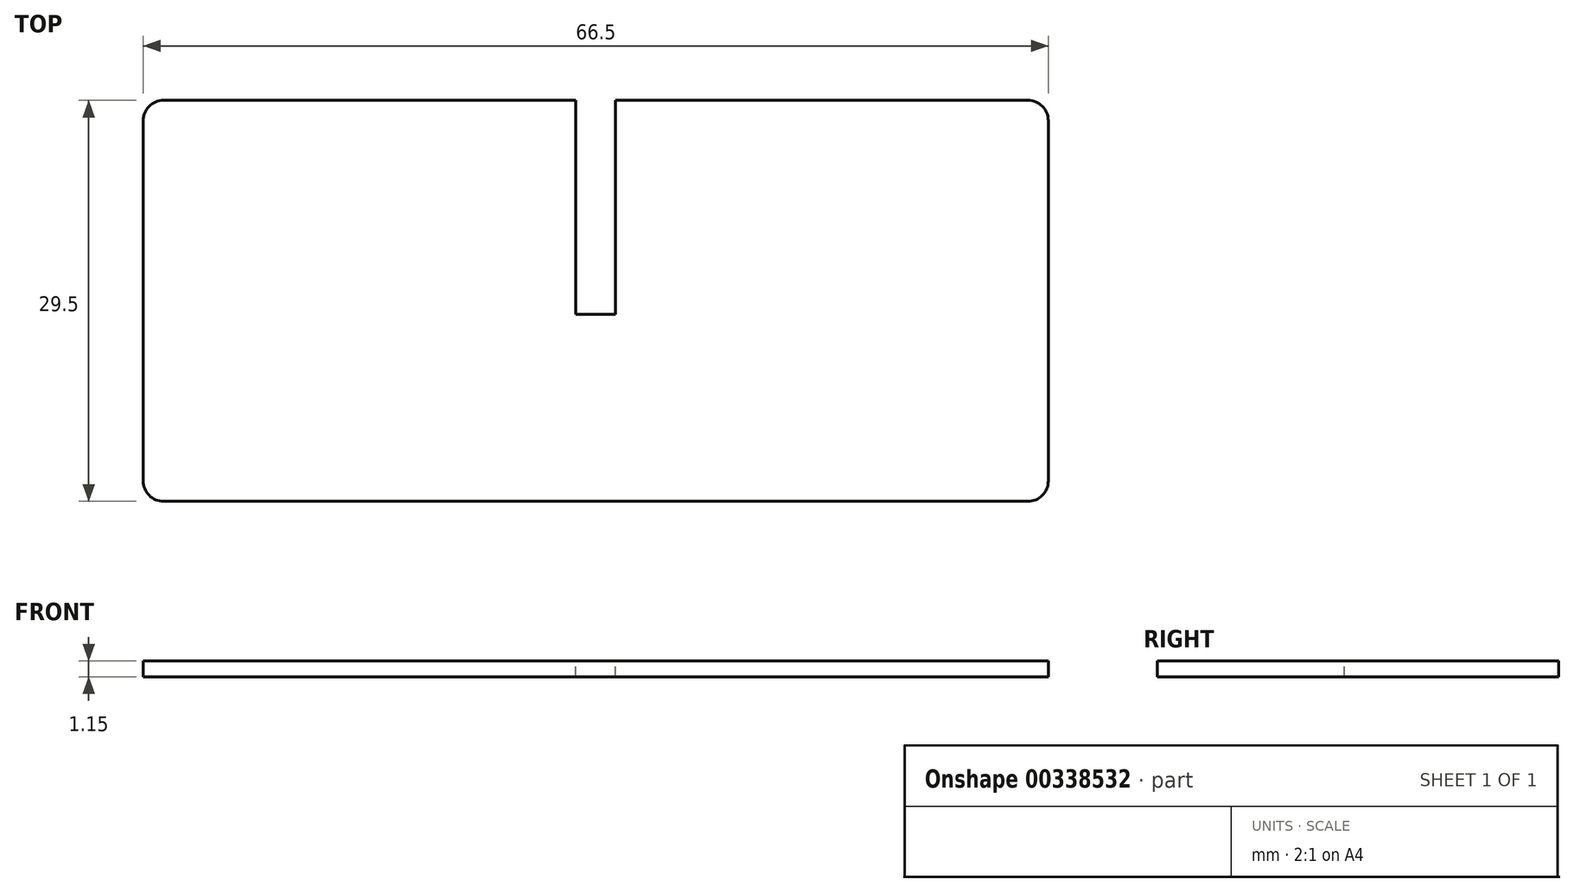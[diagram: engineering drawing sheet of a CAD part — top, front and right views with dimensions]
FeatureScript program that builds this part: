
annotation { "Feature Type Name" : "Feature", "Feature Type Description" : "" }
export const myFeature = defineFeature(function(context is Context, id is Id, definition is map)
    precondition{}
    {
        {
            var Q0;
            Q0=qCreatedBy(makeId("Top.planeOp"),FACE);
            var sketch = newSketch(context, id + "F0", { "sketchPlane" : qUnion([Q0])});
            skLineSegment(sketch, "E0.bottom", {"start": v(31.75, 14.75) * mm, "end": v(-31.75, 14.75) * mm});
            skLineSegment(sketch, "E0.top", {"start": v(31.75, -14.75) * mm, "end": v(-31.75, -14.75) * mm});
            skLineSegment(sketch, "E0.left", {"start": v(33.25, 13.25) * mm, "end": v(33.25, -13.25) * mm});
            skLineSegment(sketch, "E0.right", {"start": v(-33.25, 13.25) * mm, "end": v(-33.25, -13.25) * mm});
            skPoint(sketch, "E0.middle", {"position": v(0, 0) * mm});
            skPoint(sketch, "E1.visualSharp", {"position": v(-33.25, 14.75) * mm});
            skArc(sketch, "E1.filletArc", {"start": v(-31.75, 14.75) * mm, "mid": v(-32.81, 14.31) * mm, "end": v(-33.25, 13.25) * mm});
            skPoint(sketch, "E2.visualSharp", {"position": v(33.25, 14.75) * mm});
            skArc(sketch, "E2.filletArc", {"start": v(33.25, 13.25) * mm, "mid": v(32.81, 14.31) * mm, "end": v(31.75, 14.75) * mm});
            skPoint(sketch, "E3.visualSharp", {"position": v(33.25, -14.75) * mm});
            skArc(sketch, "E3.filletArc", {"start": v(31.75, -14.75) * mm, "mid": v(32.81, -14.31) * mm, "end": v(33.25, -13.25) * mm});
            skPoint(sketch, "E4.visualSharp", {"position": v(-33.25, -14.75) * mm});
            skArc(sketch, "E4.filletArc", {"start": v(-33.25, -13.25) * mm, "mid": v(-32.81, -14.31) * mm, "end": v(-31.75, -14.75) * mm});
            skSolve(sketch);
        }
        {
            var Q0;
            Q0=makeQuery(id+"F0.imprint","IMPRINT",FACE,{"disambiguationData":[TD([[makeQuery(id+"F0.imprint","IMPRINT",EDGE,{"derivedFrom":sQuery(id+"F0.wireOp",EDGE,"E0.bottom")}),1.0]])]});
            extrude(context, id + "F1", {"entities" : qUnion([Q0]), "depth" : 1.15 * mm});
        }
        {
            var Q0;
            Q0=makeQuery(id+"F1.opExtrude","CAP_FACE",FACE,{"disambiguationData":[OSD([sQuery(id+"F0.wireOp",EDGE,"E0.bottom"),sQuery(id+"F0.wireOp",EDGE,"E0.top"),sQuery(id+"F0.wireOp",EDGE,"E0.left"),sQuery(id+"F0.wireOp",EDGE,"E0.right"),sQuery(id+"F0.wireOp",EDGE,"E1.filletArc"),sQuery(id+"F0.wireOp",EDGE,"E2.filletArc"),sQuery(id+"F0.wireOp",EDGE,"E3.filletArc"),sQuery(id+"F0.wireOp",EDGE,"E4.filletArc")])],"isStart":false});
            var sketch = newSketch(context, id + "F2", { "sketchPlane" : qUnion([Q0])});
            skLineSegment(sketch, "E5.bottom", {"start": v(1.46, -1) * mm, "end": v(-1.46, -1) * mm});
            skLineSegment(sketch, "E5.top", {"start": v(1.46, 14.75) * mm, "end": v(-1.46, 14.75) * mm});
            skLineSegment(sketch, "E5.left", {"start": v(1.46, -1) * mm, "end": v(1.46, 14.75) * mm});
            skLineSegment(sketch, "E5.right", {"start": v(-1.46, -1) * mm, "end": v(-1.46, 14.75) * mm});
            skPoint(sketch, "E5.middle", {"position": v(0, 6.88) * mm});
            skSolve(sketch);
        }
        {
            var Q0;
            Q0=makeQuery(id+"F2.imprint","IMPRINT",FACE,{"disambiguationData":[TD([[makeQuery(id+"F2.imprint","IMPRINT",EDGE,{"derivedFrom":sQuery(id+"F2.wireOp",EDGE,"E5.bottom")}),-1.0]])]});
            extrude(context, id + "F3", {"entities" : qUnion([Q0]), "operationType" : NewBodyOperationType.REMOVE, "oppositeDirection" : true, "depth" : 25 * mm});
        }
    });
